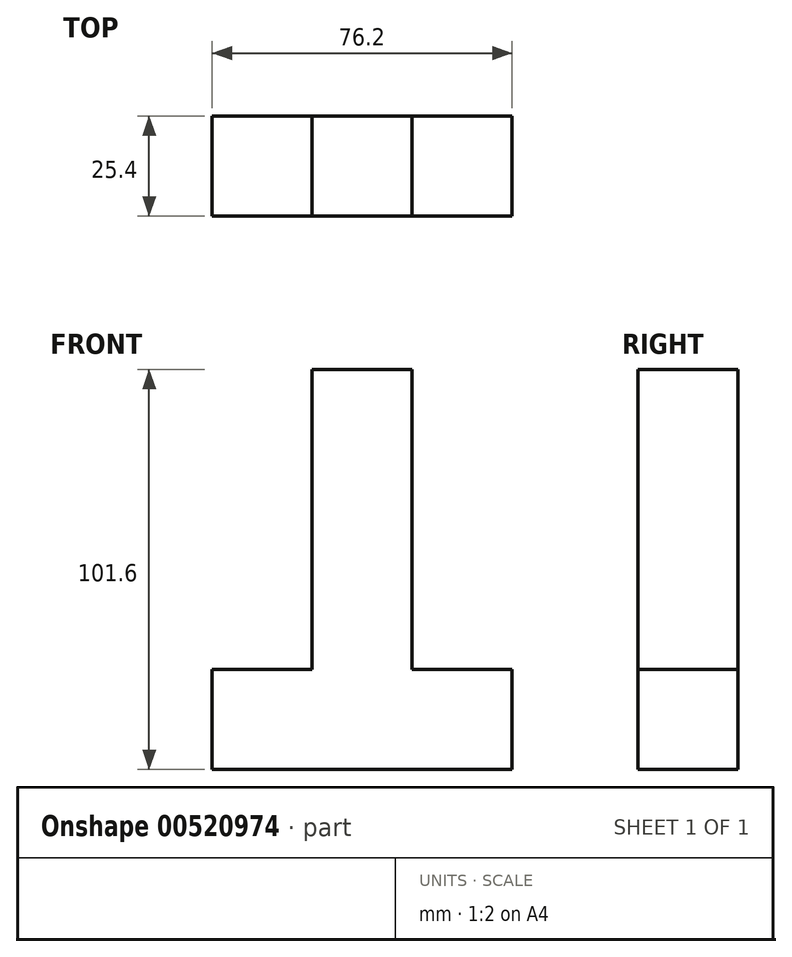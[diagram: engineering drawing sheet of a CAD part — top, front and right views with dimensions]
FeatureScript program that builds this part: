
annotation { "Feature Type Name" : "Feature", "Feature Type Description" : "" }
export const myFeature = defineFeature(function(context is Context, id is Id, definition is map)
    precondition{}
    {
        {
            var Q0;
            Q0=qCreatedBy(makeId("Front.planeOp"),FACE);
            var sketch = newSketch(context, id + "F0", { "sketchPlane" : qUnion([Q0])});
            skLineSegment(sketch, "E0", {"start": v(-25.4, 0) * mm, "end": v(-25.4, -25.4) * mm});
            skLineSegment(sketch, "E1", {"start": v(-25.4, -25.4) * mm, "end": v(0, -25.4) * mm});
            skLineSegment(sketch, "E2", {"start": v(0, -25.4) * mm, "end": v(0, 0) * mm});
            skLineSegment(sketch, "E3", {"start": v(0, 0) * mm, "end": v(-25.4, 0) * mm});
            skSolve(sketch);
        }
        {
            var Q0;
            Q0=makeQuery(id+"F0.imprint","IMPRINT",FACE,{"disambiguationData":[TD([[makeQuery(id+"F0.imprint","IMPRINT",EDGE,{"derivedFrom":sQuery(id+"F0.wireOp",EDGE,"E0")}),1.0]])]});
            extrude(context, id + "F1", {"entities" : qUnion([Q0]), "depth" : 25.4 * mm, "offsetDistance" : 25.4 * mm});
        }
        {
            var Q0;
            Q0=qCreatedBy(makeId("Front.planeOp"),FACE);
            var sketch = newSketch(context, id + "F2", { "sketchPlane" : qUnion([Q0])});
            skLineSegment(sketch, "E4", {"start": v(0, 0) * mm, "end": v(50.8, 0) * mm});
            skLineSegment(sketch, "E5", {"start": v(50.8, 0) * mm, "end": v(50.8, -25.4) * mm});
            skLineSegment(sketch, "E6", {"start": v(50.8, -25.4) * mm, "end": v(0, -25.4) * mm});
            skLineSegment(sketch, "E7", {"start": v(0, -25.4) * mm, "end": v(25.4, -25.4) * mm});
            skLineSegment(sketch, "E8", {"start": v(25.4, -25.4) * mm, "end": v(50.8, -25.4) * mm});
            skLineSegment(sketch, "E9", {"start": v(0, 0) * mm, "end": v(0, 76.2) * mm});
            skLineSegment(sketch, "E10", {"start": v(0, 76.2) * mm, "end": v(25.4, 76.2) * mm});
            skLineSegment(sketch, "E11", {"start": v(25.4, 76.2) * mm, "end": v(25.4, 0) * mm});
            skLineSegment(sketch, "E12", {"start": v(0, 0) * mm, "end": v(0, -25.4) * mm});
            skSolve(sketch);
        }
        {
            var Q0;
            {var subQ0=sQuery(id+"F2.wireOp",EDGE,"E5");Q0=makeQuery(id+"F2.imprint","IMPRINT",FACE,{"disambiguationData":[TD([[makeQuery(id+"F2.imprint","IMPRINT",EDGE,{"derivedFrom":subQ0}),-1.0]])]});}
            var Q1;
            {var subQ0=sQuery(id+"F2.wireOp",EDGE,"E9");Q1=makeQuery(id+"F2.imprint","IMPRINT",FACE,{"disambiguationData":[TD([[makeQuery(id+"F2.imprint","IMPRINT",EDGE,{"derivedFrom":subQ0}),-1.0]])]});}
            extrude(context, id + "F3", {"entities" : qUnion([Q0, Q1]), "operationType" : NewBodyOperationType.ADD, "depth" : 25.4 * mm, "offsetDistance" : 25.4 * mm});
        }
    });
